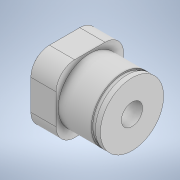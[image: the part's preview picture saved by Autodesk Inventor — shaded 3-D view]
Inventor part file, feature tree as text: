
AUTODESK INVENTOR PART (.ipt)
format: ipt  version: 2020 (Build 240168000, 168)  size: 347,136 bytes
history: native  units: mm
features: extrude x7, sketch x7, fillet x2
ambient origin geometry x8: Origin, YZ Plane, XZ Plane, XY Plane, X Axis, Y Axis, Z Axis, Center Point
bodies: Solid1 (feature_tree)
feature tree (16):
  extrude  "Extrusion1"  Depth=20.32mm
  extrude  "Extrusion2"  Depth=12.7mm
  fillet  "Fillet1"  Radius=12.7mm
  extrude  "Extrusion3"  Depth=5.588mm
  extrude  "Extrusion4"  Depth=1.5mm TaperAngle=0.0deg
  extrude  "Extrusion5"  Depth=25.0mm TaperAngle=0.0deg
  extrude  "Extrusion6"  Depth=5.0mm TaperAngle=0.0deg
  fillet  "Fillet2"  Radius=2.0mm
  extrude  "Extrusion7"  Depth=25.32mm TaperAngle=0.0deg
  sketch  "Sketch1"  dims[d0=20.32mm d1=20.32mm]
  sketch  "Sketch2"  dims[d2=7.62mm d3=0.0mm d4=19.05mm d5=12.7mm d6=0.0mm]
  sketch  "Sketch3"  dims[d7=5.588mm d8=18.25mm]
  sketch  "Sketch4"  dims[d9=2.72mm d10=0.0mm d11=1.5mm d12=0.0mm]
  sketch  "Sketch5"  dims[d13=8.0mm d14=25.0mm d15=0.0mm]
  sketch  "Sketch6"  dims[d16=10.0mm d17=5.0mm d18=0.0mm d19=2.0mm]
  sketch  "Sketch7"  dims[d20=6.4mm d21=25.32mm d22=0.0mm]
